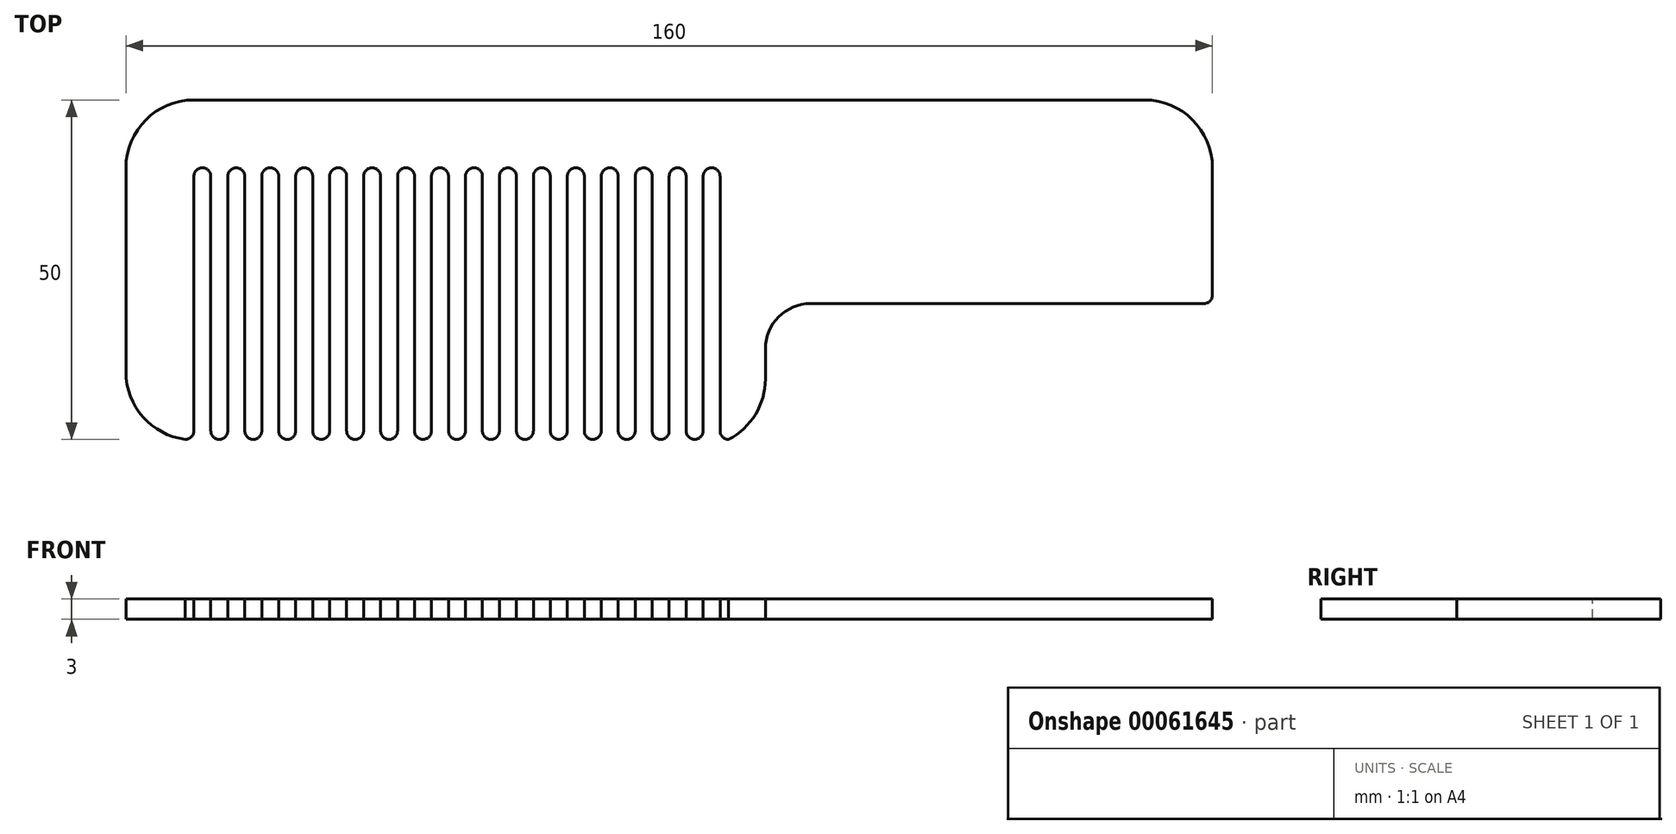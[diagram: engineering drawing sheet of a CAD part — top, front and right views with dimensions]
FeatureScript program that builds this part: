
annotation { "Feature Type Name" : "Feature", "Feature Type Description" : "" }
export const myFeature = defineFeature(function(context is Context, id is Id, definition is map)
    precondition{}
    {
        {
            assignVariable(context, id + "F0", {"name" : "Unit", "anyValue" : 10});
        }
        {
            var Q0;
            Q0=qCreatedBy(makeId("Top.planeOp"),FACE);
            var sketch = newSketch(context, id + "F1", { "sketchPlane" : qUnion([Q0])});
            skLineSegment(sketch, "E0", {"start": v(0, 0) * mm, "end": v(10, 0) * mm});
            skLineSegment(sketch, "E1", {"start": v(10, 0) * mm, "end": v(10, 40) * mm});
            skLineSegment(sketch, "E2", {"start": v(10, 40) * mm, "end": v(90, 40) * mm});
            skLineSegment(sketch, "E3", {"start": v(90, 40) * mm, "end": v(90, 0) * mm});
            skLineSegment(sketch, "E4", {"start": v(160, 20) * mm, "end": v(160, 50) * mm});
            skLineSegment(sketch, "E5", {"start": v(160, 50) * mm, "end": v(0, 50) * mm});
            skLineSegment(sketch, "E6", {"start": v(0, 50) * mm, "end": v(0, 0) * mm});
            skLineSegment(sketch, "E7", {"start": v(12.5, 40) * mm, "end": v(12.5, 0) * mm});
            skLineSegment(sketch, "E8", {"start": v(12.5, 0) * mm, "end": v(15, 0) * mm});
            skLineSegment(sketch, "E9", {"start": v(15, 0) * mm, "end": v(15, 40) * mm});
            skLineSegment(sketch, "E10.1.0.0", {"start": v(17.5, 0) * mm, "end": v(20, 0) * mm});
            skLineSegment(sketch, "E10.1.0.1", {"start": v(17.5, 40) * mm, "end": v(17.5, 0) * mm});
            skLineSegment(sketch, "E10.1.0.2", {"start": v(20, 0) * mm, "end": v(20, 40) * mm});
            skLineSegment(sketch, "E10.2.0.0", {"start": v(22.5, 0) * mm, "end": v(25, 0) * mm});
            skLineSegment(sketch, "E10.2.0.1", {"start": v(22.5, 40) * mm, "end": v(22.5, 0) * mm});
            skLineSegment(sketch, "E10.2.0.2", {"start": v(25, 0) * mm, "end": v(25, 40) * mm});
            skLineSegment(sketch, "E10.direction1", {"start": v(12.5, 0) * mm, "end": v(17.5, 0) * mm, "construction": true});
            skLineSegment(sketch, "E11.0.3.0", {"start": v(27.5, 0) * mm, "end": v(30, 0) * mm});
            skLineSegment(sketch, "E11.3.3.0", {"start": v(27.5, 40) * mm, "end": v(27.5, 0) * mm});
            skLineSegment(sketch, "E11.6.3.0", {"start": v(30, 0) * mm, "end": v(30, 40) * mm});
            skLineSegment(sketch, "E11.0.4.0", {"start": v(32.5, 0) * mm, "end": v(35, 0) * mm});
            skLineSegment(sketch, "E11.3.4.0", {"start": v(32.5, 40) * mm, "end": v(32.5, 0) * mm});
            skLineSegment(sketch, "E11.6.4.0", {"start": v(35, 0) * mm, "end": v(35, 40) * mm});
            skLineSegment(sketch, "E11.0.5.0", {"start": v(37.5, 0) * mm, "end": v(40, 0) * mm});
            skLineSegment(sketch, "E11.3.5.0", {"start": v(37.5, 40) * mm, "end": v(37.5, 0) * mm});
            skLineSegment(sketch, "E11.6.5.0", {"start": v(40, 0) * mm, "end": v(40, 40) * mm});
            skLineSegment(sketch, "E11.0.6.0", {"start": v(42.5, 0) * mm, "end": v(45, 0) * mm});
            skLineSegment(sketch, "E11.3.6.0", {"start": v(42.5, 40) * mm, "end": v(42.5, 0) * mm});
            skLineSegment(sketch, "E11.6.6.0", {"start": v(45, 0) * mm, "end": v(45, 40) * mm});
            skLineSegment(sketch, "E11.0.7.0", {"start": v(47.5, 0) * mm, "end": v(50, 0) * mm});
            skLineSegment(sketch, "E11.3.7.0", {"start": v(47.5, 40) * mm, "end": v(47.5, 0) * mm});
            skLineSegment(sketch, "E11.6.7.0", {"start": v(50, 0) * mm, "end": v(50, 40) * mm});
            skLineSegment(sketch, "E12.0.8.0", {"start": v(52.5, 0) * mm, "end": v(55, 0) * mm});
            skLineSegment(sketch, "E12.3.8.0", {"start": v(52.5, 40) * mm, "end": v(52.5, 0) * mm});
            skLineSegment(sketch, "E12.6.8.0", {"start": v(55, 0) * mm, "end": v(55, 40) * mm});
            skLineSegment(sketch, "E12.0.9.0", {"start": v(57.5, 0) * mm, "end": v(60, 0) * mm});
            skLineSegment(sketch, "E12.3.9.0", {"start": v(57.5, 40) * mm, "end": v(57.5, 0) * mm});
            skLineSegment(sketch, "E12.6.9.0", {"start": v(60, 0) * mm, "end": v(60, 40) * mm});
            skLineSegment(sketch, "E13.0.10.0", {"start": v(62.5, 0) * mm, "end": v(65, 0) * mm});
            skLineSegment(sketch, "E13.3.10.0", {"start": v(62.5, 40) * mm, "end": v(62.5, 0) * mm});
            skLineSegment(sketch, "E13.6.10.0", {"start": v(65, 0) * mm, "end": v(65, 40) * mm});
            skLineSegment(sketch, "E14.0.11.0", {"start": v(67.5, 0) * mm, "end": v(70, 0) * mm});
            skLineSegment(sketch, "E14.3.11.0", {"start": v(67.5, 40) * mm, "end": v(67.5, 0) * mm});
            skLineSegment(sketch, "E14.6.11.0", {"start": v(70, 0) * mm, "end": v(70, 40) * mm});
            skLineSegment(sketch, "E14.0.12.0", {"start": v(72.5, 0) * mm, "end": v(75, 0) * mm});
            skLineSegment(sketch, "E14.3.12.0", {"start": v(72.5, 40) * mm, "end": v(72.5, 0) * mm});
            skLineSegment(sketch, "E14.6.12.0", {"start": v(75, 0) * mm, "end": v(75, 40) * mm});
            skLineSegment(sketch, "E14.0.13.0", {"start": v(77.5, 0) * mm, "end": v(80, 0) * mm});
            skLineSegment(sketch, "E14.3.13.0", {"start": v(77.5, 40) * mm, "end": v(77.5, 0) * mm});
            skLineSegment(sketch, "E14.6.13.0", {"start": v(80, 0) * mm, "end": v(80, 40) * mm});
            skLineSegment(sketch, "E14.0.14.0", {"start": v(82.5, 0) * mm, "end": v(85, 0) * mm});
            skLineSegment(sketch, "E14.3.14.0", {"start": v(82.5, 40) * mm, "end": v(82.5, 0) * mm});
            skLineSegment(sketch, "E14.6.14.0", {"start": v(85, 0) * mm, "end": v(85, 40) * mm});
            skLineSegment(sketch, "E15.0.15.0", {"start": v(87.5, 0) * mm, "end": v(90, 0) * mm});
            skLineSegment(sketch, "E15.3.15.0", {"start": v(87.5, 40) * mm, "end": v(87.5, 0) * mm});
            skLineSegment(sketch, "E15.6.15.0", {"start": v(90, 0) * mm, "end": v(90, 40) * mm});
            skLineSegment(sketch, "E16", {"start": v(90, 20) * mm, "end": v(160, 20) * mm});
            skLineSegment(sketch, "E17", {"start": v(90, 0) * mm, "end": v(94.17, 0) * mm});
            skLineSegment(sketch, "E18", {"start": v(94.17, 0) * mm, "end": v(94.17, 20) * mm});
            skSolve(sketch);
        }
        {
            assignVariable(context, id + "F2", {"name" : "Thickness", "anyValue" : 3});
        }
        {
            var Q0;
            {var subQ0=sQuery(id+"F1.wireOp",EDGE,"E11.3.5.0");Q0=makeQuery(id+"F1.imprint","IMPRINT",FACE,{"disambiguationData":[TD([[makeQuery(id+"F1.imprint","IMPRINT",EDGE,{"derivedFrom":subQ0}),1.0]])]});}
            var Q1;
            {var subQ0=sQuery(id+"F1.wireOp",EDGE,"E11.6.3.0");Q1=makeQuery(id+"F1.imprint","IMPRINT",FACE,{"disambiguationData":[TD([[makeQuery(id+"F1.imprint","IMPRINT",EDGE,{"derivedFrom":subQ0}),-1.0]])]});}
            var Q2;
            {var subQ0=sQuery(id+"F1.wireOp",EDGE,"E11.3.3.0");Q2=makeQuery(id+"F1.imprint","IMPRINT",FACE,{"disambiguationData":[TD([[makeQuery(id+"F1.imprint","IMPRINT",EDGE,{"derivedFrom":subQ0}),1.0]])]});}
            var Q3;
            {var subQ0=sQuery(id+"F1.wireOp",EDGE,"E10.2.0.1");Q3=makeQuery(id+"F1.imprint","IMPRINT",FACE,{"disambiguationData":[TD([[makeQuery(id+"F1.imprint","IMPRINT",EDGE,{"derivedFrom":subQ0}),1.0]])]});}
            var Q4;
            {var subQ0=sQuery(id+"F1.wireOp",EDGE,"E1");Q4=makeQuery(id+"F1.imprint","IMPRINT",FACE,{"disambiguationData":[TD([[makeQuery(id+"F1.imprint","IMPRINT",EDGE,{"derivedFrom":subQ0}),-1.0]])]});}
            var Q5;
            {var subQ0=sQuery(id+"F1.wireOp",EDGE,"E10.2.0.2");Q5=makeQuery(id+"F1.imprint","IMPRINT",FACE,{"disambiguationData":[TD([[makeQuery(id+"F1.imprint","IMPRINT",EDGE,{"derivedFrom":subQ0}),-1.0]])]});}
            var Q6;
            {var subQ0=sQuery(id+"F1.wireOp",EDGE,"E10.1.0.2");Q6=makeQuery(id+"F1.imprint","IMPRINT",FACE,{"disambiguationData":[TD([[makeQuery(id+"F1.imprint","IMPRINT",EDGE,{"derivedFrom":subQ0}),-1.0]])]});}
            var Q7;
            {var subQ0=sQuery(id+"F1.wireOp",EDGE,"E14.6.12.0");Q7=makeQuery(id+"F1.imprint","IMPRINT",FACE,{"disambiguationData":[TD([[makeQuery(id+"F1.imprint","IMPRINT",EDGE,{"derivedFrom":subQ0}),-1.0]])]});}
            var Q8;
            {var subQ0=sQuery(id+"F1.wireOp",EDGE,"E10.1.0.1");Q8=makeQuery(id+"F1.imprint","IMPRINT",FACE,{"disambiguationData":[TD([[makeQuery(id+"F1.imprint","IMPRINT",EDGE,{"derivedFrom":subQ0}),1.0]])]});}
            var Q9;
            Q9=makeQuery(id+"F1.imprint","IMPRINT",FACE,{"disambiguationData":[TD([[makeQuery(id+"F1.imprint","IMPRINT",EDGE,{"derivedFrom":sQuery(id+"F1.wireOp",EDGE,"E0")}),1.0]])]});
            var Q10;
            {var subQ0=sQuery(id+"F1.wireOp",EDGE,"E9");Q10=makeQuery(id+"F1.imprint","IMPRINT",FACE,{"disambiguationData":[TD([[makeQuery(id+"F1.imprint","IMPRINT",EDGE,{"derivedFrom":subQ0}),-1.0]])]});}
            var Q11;
            {var subQ0=sQuery(id+"F1.wireOp",EDGE,"E7");Q11=makeQuery(id+"F1.imprint","IMPRINT",FACE,{"disambiguationData":[TD([[makeQuery(id+"F1.imprint","IMPRINT",EDGE,{"derivedFrom":subQ0}),1.0]])]});}
            var Q12;
            {var subQ0=sQuery(id+"F1.wireOp",EDGE,"E12.3.8.0");Q12=makeQuery(id+"F1.imprint","IMPRINT",FACE,{"disambiguationData":[TD([[makeQuery(id+"F1.imprint","IMPRINT",EDGE,{"derivedFrom":subQ0}),1.0]])]});}
            var Q13;
            {var subQ0=sQuery(id+"F1.wireOp",EDGE,"E11.3.6.0");Q13=makeQuery(id+"F1.imprint","IMPRINT",FACE,{"disambiguationData":[TD([[makeQuery(id+"F1.imprint","IMPRINT",EDGE,{"derivedFrom":subQ0}),1.0]])]});}
            var Q14;
            {var subQ0=sQuery(id+"F1.wireOp",EDGE,"E11.3.7.0");Q14=makeQuery(id+"F1.imprint","IMPRINT",FACE,{"disambiguationData":[TD([[makeQuery(id+"F1.imprint","IMPRINT",EDGE,{"derivedFrom":subQ0}),1.0]])]});}
            var Q15;
            {var subQ2=sQuery(id+"F1.wireOp",EDGE,"E15.3.15.0");Q15=makeQuery(id+"F1.imprint","IMPRINT",FACE,{"disambiguationData":[TD([[makeQuery(id+"F1.imprint","IMPRINT",EDGE,{"derivedFrom":subQ2}),1.0]])]});}
            var Q16;
            {var subQ0=sQuery(id+"F1.wireOp",EDGE,"E11.6.5.0");Q16=makeQuery(id+"F1.imprint","IMPRINT",FACE,{"disambiguationData":[TD([[makeQuery(id+"F1.imprint","IMPRINT",EDGE,{"derivedFrom":subQ0}),-1.0]])]});}
            var Q17;
            {var subQ0=sQuery(id+"F1.wireOp",EDGE,"E14.3.11.0");Q17=makeQuery(id+"F1.imprint","IMPRINT",FACE,{"disambiguationData":[TD([[makeQuery(id+"F1.imprint","IMPRINT",EDGE,{"derivedFrom":subQ0}),1.0]])]});}
            var Q18;
            {var subQ0=sQuery(id+"F1.wireOp",EDGE,"E12.3.9.0");Q18=makeQuery(id+"F1.imprint","IMPRINT",FACE,{"disambiguationData":[TD([[makeQuery(id+"F1.imprint","IMPRINT",EDGE,{"derivedFrom":subQ0}),1.0]])]});}
            var Q19;
            {var subQ0=sQuery(id+"F1.wireOp",EDGE,"E14.6.13.0");Q19=makeQuery(id+"F1.imprint","IMPRINT",FACE,{"disambiguationData":[TD([[makeQuery(id+"F1.imprint","IMPRINT",EDGE,{"derivedFrom":subQ0}),-1.0]])]});}
            var Q20;
            {var subQ0=sQuery(id+"F1.wireOp",EDGE,"E11.6.7.0");Q20=makeQuery(id+"F1.imprint","IMPRINT",FACE,{"disambiguationData":[TD([[makeQuery(id+"F1.imprint","IMPRINT",EDGE,{"derivedFrom":subQ0}),-1.0]])]});}
            var Q21;
            {var subQ0=sQuery(id+"F1.wireOp",EDGE,"E12.6.8.0");Q21=makeQuery(id+"F1.imprint","IMPRINT",FACE,{"disambiguationData":[TD([[makeQuery(id+"F1.imprint","IMPRINT",EDGE,{"derivedFrom":subQ0}),-1.0]])]});}
            var Q22;
            {var subQ0=sQuery(id+"F1.wireOp",EDGE,"E14.3.12.0");Q22=makeQuery(id+"F1.imprint","IMPRINT",FACE,{"disambiguationData":[TD([[makeQuery(id+"F1.imprint","IMPRINT",EDGE,{"derivedFrom":subQ0}),1.0]])]});}
            var Q23;
            {var subQ0=sQuery(id+"F1.wireOp",EDGE,"E14.3.13.0");Q23=makeQuery(id+"F1.imprint","IMPRINT",FACE,{"disambiguationData":[TD([[makeQuery(id+"F1.imprint","IMPRINT",EDGE,{"derivedFrom":subQ0}),1.0]])]});}
            var Q24;
            {var subQ0=sQuery(id+"F1.wireOp",EDGE,"E13.6.10.0");Q24=makeQuery(id+"F1.imprint","IMPRINT",FACE,{"disambiguationData":[TD([[makeQuery(id+"F1.imprint","IMPRINT",EDGE,{"derivedFrom":subQ0}),-1.0]])]});}
            var Q25;
            {var subQ0=sQuery(id+"F1.wireOp",EDGE,"E14.3.14.0");Q25=makeQuery(id+"F1.imprint","IMPRINT",FACE,{"disambiguationData":[TD([[makeQuery(id+"F1.imprint","IMPRINT",EDGE,{"derivedFrom":subQ0}),1.0]])]});}
            var Q26;
            {var subQ0=sQuery(id+"F1.wireOp",EDGE,"E11.6.4.0");Q26=makeQuery(id+"F1.imprint","IMPRINT",FACE,{"disambiguationData":[TD([[makeQuery(id+"F1.imprint","IMPRINT",EDGE,{"derivedFrom":subQ0}),-1.0]])]});}
            var Q27;
            {var subQ0=sQuery(id+"F1.wireOp",EDGE,"E11.3.4.0");Q27=makeQuery(id+"F1.imprint","IMPRINT",FACE,{"disambiguationData":[TD([[makeQuery(id+"F1.imprint","IMPRINT",EDGE,{"derivedFrom":subQ0}),1.0]])]});}
            var Q28;
            {var subQ0=sQuery(id+"F1.wireOp",EDGE,"E12.6.9.0");Q28=makeQuery(id+"F1.imprint","IMPRINT",FACE,{"disambiguationData":[TD([[makeQuery(id+"F1.imprint","IMPRINT",EDGE,{"derivedFrom":subQ0}),-1.0]])]});}
            var Q29;
            {var subQ0=sQuery(id+"F1.wireOp",EDGE,"E11.6.6.0");Q29=makeQuery(id+"F1.imprint","IMPRINT",FACE,{"disambiguationData":[TD([[makeQuery(id+"F1.imprint","IMPRINT",EDGE,{"derivedFrom":subQ0}),-1.0]])]});}
            var Q30;
            {var subQ0=sQuery(id+"F1.wireOp",EDGE,"E13.3.10.0");Q30=makeQuery(id+"F1.imprint","IMPRINT",FACE,{"disambiguationData":[TD([[makeQuery(id+"F1.imprint","IMPRINT",EDGE,{"derivedFrom":subQ0}),1.0]])]});}
            var Q31;
            {var subQ0=sQuery(id+"F1.wireOp",EDGE,"E14.6.14.0");Q31=makeQuery(id+"F1.imprint","IMPRINT",FACE,{"disambiguationData":[TD([[makeQuery(id+"F1.imprint","IMPRINT",EDGE,{"derivedFrom":subQ0}),-1.0]])]});}
            var Q32;
            {var subQ0=sQuery(id+"F1.wireOp",EDGE,"E14.6.11.0");Q32=makeQuery(id+"F1.imprint","IMPRINT",FACE,{"disambiguationData":[TD([[makeQuery(id+"F1.imprint","IMPRINT",EDGE,{"derivedFrom":subQ0}),-1.0]])]});}
            var Q33;
            {var subQ0=sQuery(id+"F1.wireOp",EDGE,"E17");Q33=makeQuery(id+"F1.imprint","IMPRINT",FACE,{"disambiguationData":[TD([[makeQuery(id+"F1.imprint","IMPRINT",EDGE,{"derivedFrom":subQ0}),1.0]])]});}
            extrude(context, id + "F3", {"entities" : qUnion([Q0, Q1, Q2, Q3, Q4, Q5, Q6, Q7, Q8, Q9, Q10, Q11, Q12, Q13, Q14, Q15, Q16, Q17, Q18, Q19, Q20, Q21, Q22, Q23, Q24, Q25, Q26, Q27, Q28, Q29, Q30, Q31, Q32, Q33]), "depth" : (getVariable(context, 'Thickness')) * mm});
        }
        {
            var Q0;
            Q0=makeQuery(id+"F3.opExtrude","SWEPT_EDGE",EDGE,{"disambiguationData":[OSD([sQuery(id+"F1.wireOp",EDGE,"E0"),sQuery(id+"F1.wireOp",EDGE,"E1")])]});
            var Q1;
            Q1=makeQuery(id+"F3.opExtrude","SWEPT_EDGE",EDGE,{"disambiguationData":[OSD([sQuery(id+"F1.wireOp",EDGE,"E7"),sQuery(id+"F1.wireOp",EDGE,"E8")])]});
            var Q2;
            Q2=makeQuery(id+"F3.opExtrude","SWEPT_EDGE",EDGE,{"disambiguationData":[OSD([sQuery(id+"F1.wireOp",EDGE,"E9"),sQuery(id+"F1.wireOp",EDGE,"E8")])]});
            var Q3;
            Q3=makeQuery(id+"F3.opExtrude","SWEPT_EDGE",EDGE,{"disambiguationData":[OSD([sQuery(id+"F1.wireOp",EDGE,"E10.1.0.1"),sQuery(id+"F1.wireOp",EDGE,"E10.1.0.0")])]});
            var Q4;
            Q4=makeQuery(id+"F3.opExtrude","SWEPT_EDGE",EDGE,{"disambiguationData":[OSD([sQuery(id+"F1.wireOp",EDGE,"E10.1.0.2"),sQuery(id+"F1.wireOp",EDGE,"E10.1.0.0")])]});
            var Q5;
            Q5=makeQuery(id+"F3.opExtrude","SWEPT_EDGE",EDGE,{"disambiguationData":[OSD([sQuery(id+"F1.wireOp",EDGE,"E10.2.0.1"),sQuery(id+"F1.wireOp",EDGE,"E10.2.0.0")])]});
            var Q6;
            Q6=makeQuery(id+"F3.opExtrude","SWEPT_EDGE",EDGE,{"disambiguationData":[OSD([sQuery(id+"F1.wireOp",EDGE,"E10.2.0.2"),sQuery(id+"F1.wireOp",EDGE,"E10.2.0.0")])]});
            var Q7;
            Q7=makeQuery(id+"F3.opExtrude","SWEPT_EDGE",EDGE,{"disambiguationData":[OSD([sQuery(id+"F1.wireOp",EDGE,"E11.3.3.0"),sQuery(id+"F1.wireOp",EDGE,"E11.0.3.0")])]});
            var Q8;
            Q8=makeQuery(id+"F3.opExtrude","SWEPT_EDGE",EDGE,{"disambiguationData":[OSD([sQuery(id+"F1.wireOp",EDGE,"E11.6.3.0"),sQuery(id+"F1.wireOp",EDGE,"E11.0.3.0")])]});
            var Q9;
            Q9=makeQuery(id+"F3.opExtrude","SWEPT_EDGE",EDGE,{"disambiguationData":[OSD([sQuery(id+"F1.wireOp",EDGE,"E11.3.4.0"),sQuery(id+"F1.wireOp",EDGE,"E11.0.4.0")])]});
            var Q10;
            Q10=makeQuery(id+"F3.opExtrude","SWEPT_EDGE",EDGE,{"disambiguationData":[OSD([sQuery(id+"F1.wireOp",EDGE,"E11.6.4.0"),sQuery(id+"F1.wireOp",EDGE,"E11.0.4.0")])]});
            var Q11;
            Q11=makeQuery(id+"F3.opExtrude","SWEPT_EDGE",EDGE,{"disambiguationData":[OSD([sQuery(id+"F1.wireOp",EDGE,"E11.3.5.0"),sQuery(id+"F1.wireOp",EDGE,"E11.0.5.0")])]});
            var Q12;
            Q12=makeQuery(id+"F3.opExtrude","SWEPT_EDGE",EDGE,{"disambiguationData":[OSD([sQuery(id+"F1.wireOp",EDGE,"E11.6.5.0"),sQuery(id+"F1.wireOp",EDGE,"E11.0.5.0")])]});
            var Q13;
            Q13=makeQuery(id+"F3.opExtrude","SWEPT_EDGE",EDGE,{"disambiguationData":[OSD([sQuery(id+"F1.wireOp",EDGE,"E11.3.6.0"),sQuery(id+"F1.wireOp",EDGE,"E11.0.6.0")])]});
            var Q14;
            Q14=makeQuery(id+"F3.opExtrude","SWEPT_EDGE",EDGE,{"disambiguationData":[OSD([sQuery(id+"F1.wireOp",EDGE,"E11.6.6.0"),sQuery(id+"F1.wireOp",EDGE,"E11.0.6.0")])]});
            var Q15;
            Q15=makeQuery(id+"F3.opExtrude","SWEPT_EDGE",EDGE,{"disambiguationData":[OSD([sQuery(id+"F1.wireOp",EDGE,"E11.3.7.0"),sQuery(id+"F1.wireOp",EDGE,"E11.0.7.0")])]});
            var Q16;
            Q16=makeQuery(id+"F3.opExtrude","SWEPT_EDGE",EDGE,{"disambiguationData":[OSD([sQuery(id+"F1.wireOp",EDGE,"E11.6.7.0"),sQuery(id+"F1.wireOp",EDGE,"E11.0.7.0")])]});
            var Q17;
            Q17=makeQuery(id+"F3.opExtrude","SWEPT_EDGE",EDGE,{"disambiguationData":[OSD([sQuery(id+"F1.wireOp",EDGE,"E12.3.8.0"),sQuery(id+"F1.wireOp",EDGE,"E12.0.8.0")])]});
            var Q18;
            Q18=makeQuery(id+"F3.opExtrude","SWEPT_EDGE",EDGE,{"disambiguationData":[OSD([sQuery(id+"F1.wireOp",EDGE,"E12.6.8.0"),sQuery(id+"F1.wireOp",EDGE,"E12.0.8.0")])]});
            var Q19;
            Q19=makeQuery(id+"F3.opExtrude","SWEPT_EDGE",EDGE,{"disambiguationData":[OSD([sQuery(id+"F1.wireOp",EDGE,"E12.3.9.0"),sQuery(id+"F1.wireOp",EDGE,"E12.0.9.0")])]});
            var Q20;
            Q20=makeQuery(id+"F3.opExtrude","SWEPT_EDGE",EDGE,{"disambiguationData":[OSD([sQuery(id+"F1.wireOp",EDGE,"E13.3.10.0"),sQuery(id+"F1.wireOp",EDGE,"E13.0.10.0")])]});
            var Q21;
            Q21=makeQuery(id+"F3.opExtrude","SWEPT_EDGE",EDGE,{"disambiguationData":[OSD([sQuery(id+"F1.wireOp",EDGE,"E12.6.9.0"),sQuery(id+"F1.wireOp",EDGE,"E12.0.9.0")])]});
            var Q22;
            Q22=makeQuery(id+"F3.opExtrude","SWEPT_EDGE",EDGE,{"disambiguationData":[OSD([sQuery(id+"F1.wireOp",EDGE,"E13.6.10.0"),sQuery(id+"F1.wireOp",EDGE,"E13.0.10.0")])]});
            var Q23;
            Q23=makeQuery(id+"F3.opExtrude","SWEPT_EDGE",EDGE,{"disambiguationData":[OSD([sQuery(id+"F1.wireOp",EDGE,"E14.3.11.0"),sQuery(id+"F1.wireOp",EDGE,"E14.0.11.0")])]});
            var Q24;
            Q24=makeQuery(id+"F3.opExtrude","SWEPT_EDGE",EDGE,{"disambiguationData":[OSD([sQuery(id+"F1.wireOp",EDGE,"E14.6.11.0"),sQuery(id+"F1.wireOp",EDGE,"E14.0.11.0")])]});
            var Q25;
            Q25=makeQuery(id+"F3.opExtrude","SWEPT_EDGE",EDGE,{"disambiguationData":[OSD([sQuery(id+"F1.wireOp",EDGE,"E14.3.12.0"),sQuery(id+"F1.wireOp",EDGE,"E14.0.12.0")])]});
            var Q26;
            Q26=makeQuery(id+"F3.opExtrude","SWEPT_EDGE",EDGE,{"disambiguationData":[OSD([sQuery(id+"F1.wireOp",EDGE,"E14.6.12.0"),sQuery(id+"F1.wireOp",EDGE,"E14.0.12.0")])]});
            var Q27;
            Q27=makeQuery(id+"F3.opExtrude","SWEPT_EDGE",EDGE,{"disambiguationData":[OSD([sQuery(id+"F1.wireOp",EDGE,"E14.3.13.0"),sQuery(id+"F1.wireOp",EDGE,"E14.0.13.0")])]});
            var Q28;
            Q28=makeQuery(id+"F3.opExtrude","SWEPT_EDGE",EDGE,{"disambiguationData":[OSD([sQuery(id+"F1.wireOp",EDGE,"E14.6.13.0"),sQuery(id+"F1.wireOp",EDGE,"E14.0.13.0")])]});
            var Q29;
            Q29=makeQuery(id+"F3.opExtrude","SWEPT_EDGE",EDGE,{"disambiguationData":[OSD([sQuery(id+"F1.wireOp",EDGE,"E14.3.14.0"),sQuery(id+"F1.wireOp",EDGE,"E14.0.14.0")])]});
            var Q30;
            Q30=makeQuery(id+"F3.opExtrude","SWEPT_EDGE",EDGE,{"disambiguationData":[OSD([sQuery(id+"F1.wireOp",EDGE,"E14.6.14.0"),sQuery(id+"F1.wireOp",EDGE,"E14.0.14.0")])]});
            var Q31;
            Q31=makeQuery(id+"F3.opExtrude","SWEPT_EDGE",EDGE,{"disambiguationData":[OSD([sQuery(id+"F1.wireOp",EDGE,"E15.3.15.0"),sQuery(id+"F1.wireOp",EDGE,"E15.0.15.0")])]});
            var Q32;
            Q32=makeQuery(id+"F3.opExtrude","SWEPT_EDGE",EDGE,{"disambiguationData":[OSD([sQuery(id+"F1.wireOp",EDGE,"E15.6.15.0"),sQuery(id+"F1.wireOp",EDGE,"E15.0.15.0")])]});
            var Q33;
            Q33=makeQuery(id+"F3.opExtrude","SWEPT_EDGE",EDGE,{"disambiguationData":[OSD([sQuery(id+"F1.wireOp",EDGE,"E1"),sQuery(id+"F1.wireOp",EDGE,"E2")])]});
            var Q34;
            Q34=makeQuery(id+"F3.opExtrude","SWEPT_EDGE",EDGE,{"disambiguationData":[OSD([sQuery(id+"F1.wireOp",EDGE,"E2"),sQuery(id+"F1.wireOp",EDGE,"E9")])]});
            var Q35;
            Q35=makeQuery(id+"F3.opExtrude","SWEPT_EDGE",EDGE,{"disambiguationData":[OSD([sQuery(id+"F1.wireOp",EDGE,"E2"),sQuery(id+"F1.wireOp",EDGE,"E10.1.0.2")])]});
            var Q36;
            Q36=makeQuery(id+"F3.opExtrude","SWEPT_EDGE",EDGE,{"disambiguationData":[OSD([sQuery(id+"F1.wireOp",EDGE,"E2"),sQuery(id+"F1.wireOp",EDGE,"E10.2.0.2")])]});
            var Q37;
            Q37=makeQuery(id+"F3.opExtrude","SWEPT_EDGE",EDGE,{"disambiguationData":[OSD([sQuery(id+"F1.wireOp",EDGE,"E2"),sQuery(id+"F1.wireOp",EDGE,"E11.6.3.0")])]});
            var Q38;
            Q38=makeQuery(id+"F3.opExtrude","SWEPT_EDGE",EDGE,{"disambiguationData":[OSD([sQuery(id+"F1.wireOp",EDGE,"E2"),sQuery(id+"F1.wireOp",EDGE,"E11.6.4.0")])]});
            var Q39;
            Q39=makeQuery(id+"F3.opExtrude","SWEPT_EDGE",EDGE,{"disambiguationData":[OSD([sQuery(id+"F1.wireOp",EDGE,"E2"),sQuery(id+"F1.wireOp",EDGE,"E11.6.5.0")])]});
            var Q40;
            Q40=makeQuery(id+"F3.opExtrude","SWEPT_EDGE",EDGE,{"disambiguationData":[OSD([sQuery(id+"F1.wireOp",EDGE,"E2"),sQuery(id+"F1.wireOp",EDGE,"E11.6.6.0")])]});
            var Q41;
            Q41=makeQuery(id+"F3.opExtrude","SWEPT_EDGE",EDGE,{"disambiguationData":[OSD([sQuery(id+"F1.wireOp",EDGE,"E2"),sQuery(id+"F1.wireOp",EDGE,"E11.6.7.0")])]});
            var Q42;
            Q42=makeQuery(id+"F3.opExtrude","SWEPT_EDGE",EDGE,{"disambiguationData":[OSD([sQuery(id+"F1.wireOp",EDGE,"E2"),sQuery(id+"F1.wireOp",EDGE,"E14.6.14.0")])]});
            var Q43;
            Q43=makeQuery(id+"F3.opExtrude","SWEPT_EDGE",EDGE,{"disambiguationData":[OSD([sQuery(id+"F1.wireOp",EDGE,"E2"),sQuery(id+"F1.wireOp",EDGE,"E14.6.13.0")])]});
            var Q44;
            Q44=makeQuery(id+"F3.opExtrude","SWEPT_EDGE",EDGE,{"disambiguationData":[OSD([sQuery(id+"F1.wireOp",EDGE,"E2"),sQuery(id+"F1.wireOp",EDGE,"E14.6.12.0")])]});
            var Q45;
            Q45=makeQuery(id+"F3.opExtrude","SWEPT_EDGE",EDGE,{"disambiguationData":[OSD([sQuery(id+"F1.wireOp",EDGE,"E2"),sQuery(id+"F1.wireOp",EDGE,"E14.6.11.0")])]});
            var Q46;
            Q46=makeQuery(id+"F3.opExtrude","SWEPT_EDGE",EDGE,{"disambiguationData":[OSD([sQuery(id+"F1.wireOp",EDGE,"E2"),sQuery(id+"F1.wireOp",EDGE,"E13.6.10.0")])]});
            var Q47;
            Q47=makeQuery(id+"F3.opExtrude","SWEPT_EDGE",EDGE,{"disambiguationData":[OSD([sQuery(id+"F1.wireOp",EDGE,"E2"),sQuery(id+"F1.wireOp",EDGE,"E12.6.9.0")])]});
            var Q48;
            Q48=makeQuery(id+"F3.opExtrude","SWEPT_EDGE",EDGE,{"disambiguationData":[OSD([sQuery(id+"F1.wireOp",EDGE,"E2"),sQuery(id+"F1.wireOp",EDGE,"E12.6.8.0")])]});
            var Q49;
            Q49=makeQuery(id+"F3.opExtrude","SWEPT_EDGE",EDGE,{"disambiguationData":[OSD([sQuery(id+"F1.wireOp",EDGE,"E2"),sQuery(id+"F1.wireOp",EDGE,"E15.3.15.0")])]});
            var Q50;
            Q50=makeQuery(id+"F3.opExtrude","SWEPT_EDGE",EDGE,{"disambiguationData":[OSD([sQuery(id+"F1.wireOp",EDGE,"E2"),sQuery(id+"F1.wireOp",EDGE,"E14.3.14.0")])]});
            var Q51;
            Q51=makeQuery(id+"F3.opExtrude","SWEPT_EDGE",EDGE,{"disambiguationData":[OSD([sQuery(id+"F1.wireOp",EDGE,"E2"),sQuery(id+"F1.wireOp",EDGE,"E14.3.13.0")])]});
            var Q52;
            Q52=makeQuery(id+"F3.opExtrude","SWEPT_EDGE",EDGE,{"disambiguationData":[OSD([sQuery(id+"F1.wireOp",EDGE,"E2"),sQuery(id+"F1.wireOp",EDGE,"E14.3.12.0")])]});
            var Q53;
            Q53=makeQuery(id+"F3.opExtrude","SWEPT_EDGE",EDGE,{"disambiguationData":[OSD([sQuery(id+"F1.wireOp",EDGE,"E2"),sQuery(id+"F1.wireOp",EDGE,"E14.3.11.0")])]});
            var Q54;
            Q54=makeQuery(id+"F3.opExtrude","SWEPT_EDGE",EDGE,{"disambiguationData":[OSD([sQuery(id+"F1.wireOp",EDGE,"E2"),sQuery(id+"F1.wireOp",EDGE,"E13.3.10.0")])]});
            var Q55;
            Q55=makeQuery(id+"F3.opExtrude","SWEPT_EDGE",EDGE,{"disambiguationData":[OSD([sQuery(id+"F1.wireOp",EDGE,"E2"),sQuery(id+"F1.wireOp",EDGE,"E12.3.9.0")])]});
            var Q56;
            Q56=makeQuery(id+"F3.opExtrude","SWEPT_EDGE",EDGE,{"disambiguationData":[OSD([sQuery(id+"F1.wireOp",EDGE,"E2"),sQuery(id+"F1.wireOp",EDGE,"E12.3.8.0")])]});
            var Q57;
            Q57=makeQuery(id+"F3.opExtrude","SWEPT_EDGE",EDGE,{"disambiguationData":[OSD([sQuery(id+"F1.wireOp",EDGE,"E2"),sQuery(id+"F1.wireOp",EDGE,"E11.3.7.0")])]});
            var Q58;
            Q58=makeQuery(id+"F3.opExtrude","SWEPT_EDGE",EDGE,{"disambiguationData":[OSD([sQuery(id+"F1.wireOp",EDGE,"E2"),sQuery(id+"F1.wireOp",EDGE,"E11.3.6.0")])]});
            var Q59;
            Q59=makeQuery(id+"F3.opExtrude","SWEPT_EDGE",EDGE,{"disambiguationData":[OSD([sQuery(id+"F1.wireOp",EDGE,"E2"),sQuery(id+"F1.wireOp",EDGE,"E11.3.5.0")])]});
            var Q60;
            Q60=makeQuery(id+"F3.opExtrude","SWEPT_EDGE",EDGE,{"disambiguationData":[OSD([sQuery(id+"F1.wireOp",EDGE,"E2"),sQuery(id+"F1.wireOp",EDGE,"E11.3.4.0")])]});
            var Q61;
            Q61=makeQuery(id+"F3.opExtrude","SWEPT_EDGE",EDGE,{"disambiguationData":[OSD([sQuery(id+"F1.wireOp",EDGE,"E2"),sQuery(id+"F1.wireOp",EDGE,"E11.3.3.0")])]});
            var Q62;
            Q62=makeQuery(id+"F3.opExtrude","SWEPT_EDGE",EDGE,{"disambiguationData":[OSD([sQuery(id+"F1.wireOp",EDGE,"E2"),sQuery(id+"F1.wireOp",EDGE,"E10.2.0.1")])]});
            var Q63;
            Q63=makeQuery(id+"F3.opExtrude","SWEPT_EDGE",EDGE,{"disambiguationData":[OSD([sQuery(id+"F1.wireOp",EDGE,"E2"),sQuery(id+"F1.wireOp",EDGE,"E7")])]});
            var Q64;
            Q64=makeQuery(id+"F3.opExtrude","SWEPT_EDGE",EDGE,{"disambiguationData":[OSD([sQuery(id+"F1.wireOp",EDGE,"E2"),sQuery(id+"F1.wireOp",EDGE,"E10.1.0.1")])]});
            var Q65;
            Q65=makeQuery(id+"F3.opExtrude","SWEPT_EDGE",EDGE,{"disambiguationData":[OSD([sQuery(id+"F1.wireOp",EDGE,"E4"),sQuery(id+"F1.wireOp",EDGE,"E16")])]});
            fillet(context, id + "F4", {"entities" : qUnion([Q0, Q1, Q2, Q3, Q4, Q5, Q6, Q7, Q8, Q9, Q10, Q11, Q12, Q13, Q14, Q15, Q16, Q17, Q18, Q19, Q20, Q21, Q22, Q23, Q24, Q25, Q26, Q27, Q28, Q29, Q30, Q31, Q32, Q33, Q34, Q35, Q36, Q37, Q38, Q39, Q40, Q41, Q42, Q43, Q44, Q45, Q46, Q47, Q48, Q49, Q50, Q51, Q52, Q53, Q54, Q55, Q56, Q57, Q58, Q59, Q60, Q61, Q62, Q63, Q64, Q65]), "radius" : (getVariable(context, 'Unit') / 8) * mm, "tangentPropagation" : true, "allowEdgeOverflow" : false});
        }
        {
            var Q0;
            Q0=makeQuery(id+"F3.opExtrude","SWEPT_EDGE",EDGE,{"disambiguationData":[OSD([sQuery(id+"F1.wireOp",EDGE,"E5"),sQuery(id+"F1.wireOp",EDGE,"E6")])]});
            var Q1;
            Q1=makeQuery(id+"F3.opExtrude","SWEPT_EDGE",EDGE,{"disambiguationData":[OSD([sQuery(id+"F1.wireOp",EDGE,"E0"),sQuery(id+"F1.wireOp",EDGE,"E6")])]});
            var Q2;
            Q2=makeQuery(id+"F3.opExtrude","SWEPT_EDGE",EDGE,{"disambiguationData":[OSD([sQuery(id+"F1.wireOp",EDGE,"E17"),sQuery(id+"F1.wireOp",EDGE,"E18")])]});
            var Q3;
            Q3=makeQuery(id+"F3.opExtrude","SWEPT_EDGE",EDGE,{"disambiguationData":[OSD([sQuery(id+"F1.wireOp",EDGE,"E4"),sQuery(id+"F1.wireOp",EDGE,"E5")])]});
            fillet(context, id + "F5", {"entities" : qUnion([Q0, Q1, Q2, Q3]), "radius" : (getVariable(context, 'Unit')) * mm, "allowEdgeOverflow" : false});
        }
        {
            var Q0;
            Q0=makeQuery(id+"F3.opExtrude","SWEPT_EDGE",EDGE,{"disambiguationData":[OSD([sQuery(id+"F1.wireOp",EDGE,"E16"),sQuery(id+"F1.wireOp",EDGE,"E18")])]});
            fillet(context, id + "F6", {"entities" : qUnion([Q0]), "radius" : (getVariable(context, 'Unit') * 2 / 3) * mm, "tangentPropagation" : true, "allowEdgeOverflow" : false});
        }
    });
